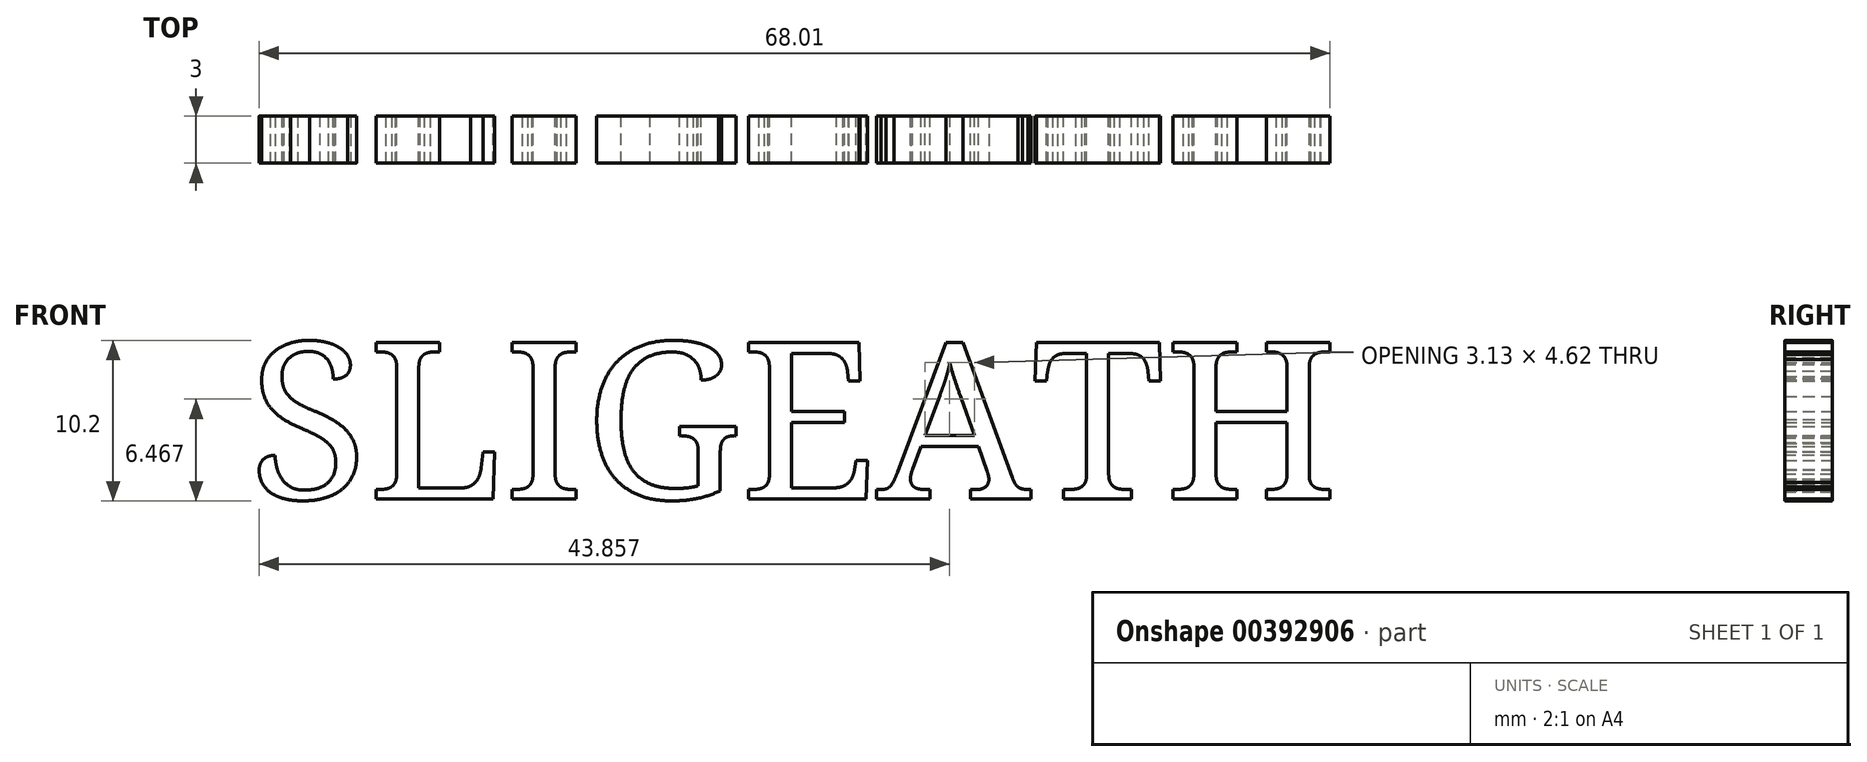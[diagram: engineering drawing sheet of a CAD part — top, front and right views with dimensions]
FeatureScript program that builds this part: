
annotation { "Feature Type Name" : "Feature", "Feature Type Description" : "" }
export const myFeature = defineFeature(function(context is Context, id is Id, definition is map)
    precondition{}
    {
        {
            var Q0;
            Q0=qCreatedBy(makeId("Front.planeOp"),FACE);
            var sketch = newSketch(context, id + "F0", { "sketchPlane" : qUnion([Q0])});
            skText(sketch, "E0", { "text": "SLIGEATH", "fontName": "NotoSerif-Regular.ttf"});
            const initialGuessF0  = {"E0": [0, 0, 1, 0, 0.01]};
            skSetInitialGuess(sketch, initialGuessF0);
            skSolve(sketch);
        }
        {
            var Q0;
            Q0 = qSketchRegion(id + "F0", true);
            extrude(context, id + "F1", {"entities" : qUnion([Q0]), "depth" : 3 * mm});
        }
    });
